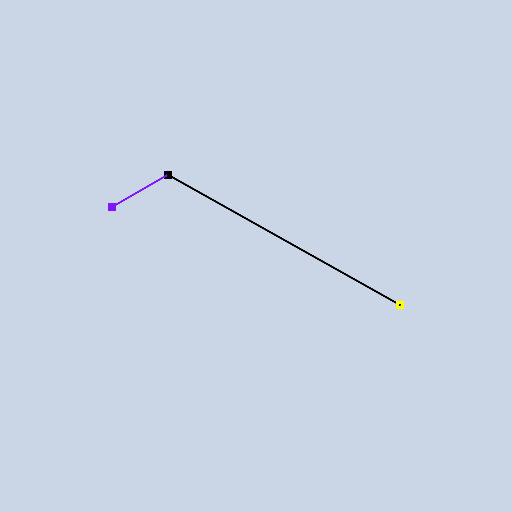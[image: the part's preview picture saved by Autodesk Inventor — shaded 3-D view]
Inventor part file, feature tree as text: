
AUTODESK INVENTOR PART (.ipt)
format: ipt  version: 2025 (Build 290162000, 162)  size: 148,992 bytes
history: native  units: in
note: dims shown in document units (in); Inventor stores cm internally (conversion verified against a paired STEP export)
features: other x2, plane x1, sketch x1
ambient origin geometry x8: Origin, YZ Plane, XZ Plane, XY Plane, X Axis, Y Axis, Z Axis, Center Point
feature tree (4):
  other  "Work Point1"
  other  "Work Point2"
  plane  "Work Plane1"
  sketch  "3D Sketch1"
